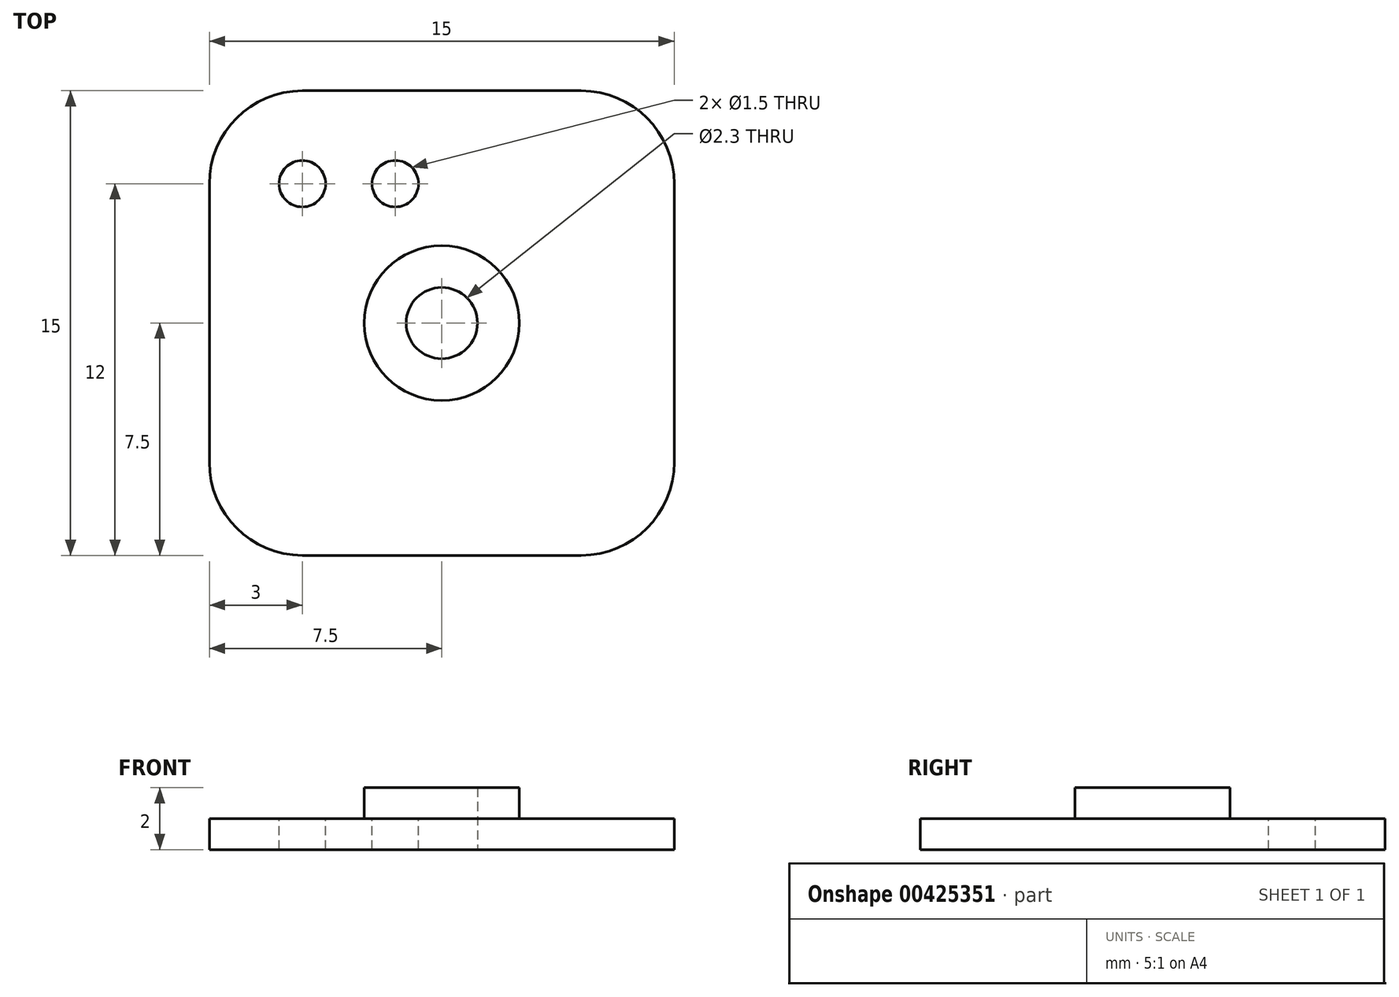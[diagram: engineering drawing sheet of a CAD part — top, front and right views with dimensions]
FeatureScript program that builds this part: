
annotation { "Feature Type Name" : "Feature", "Feature Type Description" : "" }
export const myFeature = defineFeature(function(context is Context, id is Id, definition is map)
    precondition{}
    {
        {
            var Q0;
            Q0=qCreatedBy(makeId("Top.planeOp"),FACE);
            var sketch = newSketch(context, id + "F0", { "sketchPlane" : qUnion([Q0])});
            skCircle(sketch, "E0", {"center": v(0, 0) * mm, "radius": 1.15 * mm});
            skCircle(sketch, "E1", {"center": v(0, 0) * mm, "radius": 2.5 * mm});
            skSolve(sketch);
        }
        {
            var Q0;
            Q0=makeQuery(id+"F0.imprint","IMPRINT",FACE,{"disambiguationData":[TD([[makeQuery(id+"F0.imprint","IMPRINT",EDGE,{"derivedFrom":sQuery(id+"F0.wireOp",EDGE,"E0")}),-1.0]])]});
            extrude(context, id + "F1", {"entities" : qUnion([Q0]), "depth" : 1 * mm});
        }
        {
            var Q0;
            Q0=makeQuery(id+"F1.opExtrude","CAP_FACE",FACE,{"disambiguationData":[OSD([sQuery(id+"F0.wireOp",EDGE,"E0"),sQuery(id+"F0.wireOp",EDGE,"E1")])],"isStart":true});
            var sketch = newSketch(context, id + "F2", { "sketchPlane" : qUnion([Q0])});
            skCircle(sketch, "E2", {"center": v(0, 0) * mm, "radius": 1.15 * mm});
            skCircle(sketch, "E3", {"center": v(0, 0) * mm, "radius": 5 * mm});
            skLineSegment(sketch, "E4.bottom", {"start": v(-7.5, -7.5) * mm, "end": v(7.5, -7.5) * mm});
            skLineSegment(sketch, "E4.top", {"start": v(-7.5, 7.5) * mm, "end": v(7.5, 7.5) * mm});
            skLineSegment(sketch, "E4.left", {"start": v(-7.5, -7.5) * mm, "end": v(-7.5, 7.5) * mm});
            skLineSegment(sketch, "E4.right", {"start": v(7.5, -7.5) * mm, "end": v(7.5, 7.5) * mm});
            skSolve(sketch);
        }
        {
            var Q0;
            Q0=makeQuery(id+"F2.imprint","IMPRINT",FACE,{"disambiguationData":[TD([[makeQuery(id+"F2.imprint","IMPRINT",EDGE,{"derivedFrom":sQuery(id+"F2.wireOp",EDGE,"E3")}),-1.0]])]});
            var Q1;
            Q1=makeQuery(id+"F2.imprint","IMPRINT",FACE,{"disambiguationData":[TD([[makeQuery(id+"F2.imprint","IMPRINT",EDGE,{"derivedFrom":sQuery(id+"F2.wireOp",EDGE,"E3")}),1.0]])]});
            var Q2;
            Q2=makeQuery(id+"F2.imprint","IMPRINT",FACE,{"disambiguationData":[TD([[makeQuery(id+"F2.imprint","IMPRINT",EDGE,{"derivedFrom":sQuery(id+"F2.wireOp",EDGE,"E2")}),1.0]])]});
            extrude(context, id + "F3", {"entities" : qUnion([Q0, Q1, Q2]), "operationType" : NewBodyOperationType.ADD, "depth" : 1 * mm});
        }
        {
            var Q0;
            Q0=makeQuery(id+"F3.opExtrude","SWEPT_EDGE",EDGE,{"disambiguationData":[OSD([sQuery(id+"F2.wireOp",EDGE,"E4.bottom"),sQuery(id+"F2.wireOp",EDGE,"E4.left")])]});
            var Q1;
            Q1=makeQuery(id+"F3.opExtrude","SWEPT_EDGE",EDGE,{"disambiguationData":[OSD([sQuery(id+"F2.wireOp",EDGE,"E4.bottom"),sQuery(id+"F2.wireOp",EDGE,"E4.right")])]});
            var Q2;
            Q2=makeQuery(id+"F3.opExtrude","SWEPT_EDGE",EDGE,{"disambiguationData":[OSD([sQuery(id+"F2.wireOp",EDGE,"E4.top"),sQuery(id+"F2.wireOp",EDGE,"E4.left")])]});
            var Q3;
            Q3=makeQuery(id+"F3.opExtrude","SWEPT_EDGE",EDGE,{"disambiguationData":[OSD([sQuery(id+"F2.wireOp",EDGE,"E4.top"),sQuery(id+"F2.wireOp",EDGE,"E4.right")])]});
            fillet(context, id + "F4", {"entities" : qUnion([Q0, Q1, Q2, Q3]), "radius" : 3 * mm, "tangentPropagation" : true, "allowEdgeOverflow" : false});
        }
        {
            var Q0;
            Q0=makeQuery(id+"F3.opExtrude","CAP_FACE",FACE,{"disambiguationData":[OSD([sQuery(id+"F2.wireOp",EDGE,"E2"),sQuery(id+"F2.wireOp",EDGE,"E4.bottom"),sQuery(id+"F2.wireOp",EDGE,"E4.top"),sQuery(id+"F2.wireOp",EDGE,"E4.left"),sQuery(id+"F2.wireOp",EDGE,"E4.right")])],"isStart":true});
            var sketch = newSketch(context, id + "F5", { "sketchPlane" : qUnion([Q0])});
            skCircle(sketch, "E5", {"center": v(-4.5, 4.5) * mm, "radius": 0.75 * mm});
            skCircle(sketch, "E6", {"center": v(-1.5, 4.5) * mm, "radius": 0.75 * mm});
            skSolve(sketch);
        }
        {
            var Q0;
            Q0=qSketchRegion(id+"F5",true);
            extrude(context, id + "F6", {"entities" : qUnion([Q0]), "operationType" : NewBodyOperationType.REMOVE, "oppositeDirection" : true, "depth" : 25 * mm});
        }
    });
